FCSTD DOCUMENT  (FreeCAD 0.19R)
Label: Mk8
License: All rights reserved
LicenseURL: http://en.wikipedia.org/wiki/All_rights_reserved
objects: Sketcher::SketchObject×2, PartDesign::Body×1
note: 3 computed .brp shape members not serialized (recipe doc carries the construction recipe); baked Part::Feature solids carry a one-line shape summary decoded from their .brp

FEATURE [Sketcher::SketchObject] Sketch
  FullyConstrained = false
  MapMode = 5
  sketch-geometry (53):
    g0: Circle CenterX=-353.73 CenterY=339.6 CenterZ=0 NormalX=0 NormalY=0 NormalZ=1 AngleXU=0 Radius=339.6
    g1: Circle CenterX=559.315 CenterY=339.6 CenterZ=0 NormalX=0 NormalY=0 NormalZ=1 AngleXU=0 Radius=339.6
    g2: Circle CenterX=0 CenterY=249.6 CenterZ=0 NormalX=0 NormalY=0 NormalZ=1 AngleXU=0 Radius=19
    g3: Circle CenterX=355.046 CenterY=817.792 CenterZ=0 NormalX=0 NormalY=0 NormalZ=1 AngleXU=0 Radius=11.1
    g4: Circle CenterX=0 CenterY=249.6 CenterZ=0 NormalX=0 NormalY=0 NormalZ=1 AngleXU=0 Radius=127
    g5: LineSegment StartX=510.781 StartY=339.6 StartZ=0 EndX=328.385 EndY=791.045 EndZ=0
    g6: LineSegment StartX=559.315 StartY=339.6 StartZ=0 EndX=559.315 EndY=0 EndZ=0
    g7: LineSegment StartX=510.781 StartY=339.6 StartZ=0 EndX=647.988 EndY=0 EndZ=0
    g8: LineSegment StartX=358.792 StartY=808.52 StartZ=0 EndX=324.985 EndY=799.462 EndZ=0
    g9: Circle CenterX=324.985 CenterY=799.462 CenterZ=0 NormalX=0 NormalY=0 NormalZ=1 AngleXU=0 Radius=19
    g10: Circle CenterX=335.796 CenterY=772.703 CenterZ=0 NormalX=0 NormalY=0 NormalZ=1 AngleXU=0 Radius=8
    g11: Circle CenterX=355.65 CenterY=723.562 CenterZ=0 NormalX=0 NormalY=0 NormalZ=1 AngleXU=0 Radius=45
    g12: Circle CenterX=375.13 CenterY=675.348 CenterZ=0 NormalX=0 NormalY=0 NormalZ=1 AngleXU=0 Radius=7
    g13: LineSegment StartX=-353.73 StartY=339.6 StartZ=0 EndX=559.315 EndY=339.6 EndZ=0
    g14: LineSegment StartX=-353.73 StartY=339.6 StartZ=0 EndX=-80.7377 EndY=584.568 EndZ=0
    g15: LineSegment StartX=-13.6879 StartY=474.616 StartZ=0 EndX=345.52 EndY=748.635 EndZ=0
    g16: LineSegment StartX=0 StartY=249.6 StartZ=0 EndX=358.348 EndY=716.885 EndZ=0
    g17: LineSegment StartX=559.315 StartY=0 StartZ=0 EndX=647.988 EndY=0 EndZ=0
    g18: LineSegment StartX=0 StartY=249.6 StartZ=0 EndX=355.046 EndY=817.792 EndZ=0
    g19: LineSegment StartX=-353.73 StartY=339.6 StartZ=0 EndX=0 EndY=249.6 EndZ=0
    g20: LineSegment StartX=355.046 StartY=817.792 StartZ=0 EndX=358.792 EndY=808.52 EndZ=0
    g21: Circle CenterX=332.451 CenterY=780.983 CenterZ=0 NormalX=0 NormalY=0 NormalZ=1 AngleXU=0 Radius=0.930276
    g22: LineSegment StartX=3.73444 StartY=230.971 StartZ=0 EndX=351.145 EndY=683.993 EndZ=0
    g23: LineSegment StartX=3.73444 StartY=230.971 StartZ=0 EndX=351.145 EndY=683.993 EndZ=0
    g24: LineSegment StartX=3.44458 StartY=471.712 StartZ=0 EndX=334.789 EndY=724.476 EndZ=0
    g25: LineSegment StartX=-7.54371 StartY=495.276 StartZ=0 EndX=324.922 EndY=748.896 EndZ=0
    g26: LineSegment StartX=356.409 StartY=772.403 StartZ=0 EndX=321.176 EndY=758.168 EndZ=0
    g27: LineSegment StartX=321.176 StartY=758.168 StartZ=0 EndX=354.891 EndY=674.721 EndZ=0
    g28: LineSegment StartX=354.891 StartY=674.721 StartZ=0 EndX=390.124 EndY=688.956 EndZ=0
    g29: LineSegment StartX=390.124 StartY=688.956 StartZ=0 EndX=356.409 EndY=772.403 EndZ=0
    g30: LineSegment StartX=559.315 StartY=339.6 StartZ=0 EndX=377.752 EndY=668.858 EndZ=0
    g31: LineSegment StartX=63.5524 StartY=308.973 StartZ=0 EndX=-173.714 EndY=817.792 EndZ=0
    g32: LineSegment StartX=329.613 StartY=642.256 StartZ=0 EndX=425.939 EndY=695.372 EndZ=0
    g33: LineSegment StartX=-173.714 StartY=817.792 StartZ=0 EndX=0 EndY=249.6 EndZ=0
    g34: LineSegment StartX=-303.72 StartY=817.792 StartZ=0 EndX=355.046 EndY=817.792 EndZ=0
    g35: LineSegment StartX=53.7404 StartY=296.178 StartZ=0 EndX=-103.376 EndY=633.116 EndZ=0
    g36: LineSegment StartX=-77.3814 StartY=645.043 StartZ=0 EndX=69.984 EndY=329.017 EndZ=0
    g37: LineSegment StartX=481.667 StartY=531.786 StartZ=0 EndX=559.315 EndY=339.6 EndZ=0
    g38: LineSegment StartX=36.0494 StartY=578.413 StartZ=0 EndX=36.0494 EndY=0 EndZ=0
    g39: Circle CenterX=-353.73 CenterY=339.6 CenterZ=0 NormalX=0 NormalY=0 NormalZ=1 AngleXU=0 Radius=327.5
    g40: Circle CenterX=0 CenterY=249.6 CenterZ=0 NormalX=0 NormalY=0 NormalZ=1 AngleXU=0 Radius=21
    g41: LineSegment StartX=-24.7243 StartY=255.437 StartZ=0 EndX=-20.3516 EndY=254.778 EndZ=0
    g42: LineSegment StartX=338.399 StartY=714.37 StartZ=0 EndX=-1.16744 EndY=271.577 EndZ=0
    g43: Circle CenterX=-382.93 CenterY=445.639 CenterZ=0 NormalX=0 NormalY=0 NormalZ=1 AngleXU=0 Radius=8
    g44: LineSegment StartX=-385.819 StartY=453.099 StartZ=0 EndX=325.125 EndY=750.053 EndZ=0
    g45: LineSegment StartX=329.781 StartY=734.661 StartZ=0 EndX=-379.847 EndY=438.257 EndZ=0
    g46: LineSegment StartX=-379.847 StartY=438.257 StartZ=0 EndX=339.437 EndY=716.726 EndZ=0
    g47: LineSegment StartX=-385.819 StartY=453.099 StartZ=0 EndX=330.834 EndY=730.549 EndZ=0
    g48: LineSegment StartX=0 StartY=249.6 StartZ=0 EndX=510.781 EndY=339.6 EndZ=0
    g49: LineSegment StartX=0 StartY=249.6 StartZ=0 EndX=374.387 EndY=681.775 EndZ=0
    g50: LineSegment StartX=510.781 StartY=339.6 StartZ=0 EndX=374.387 EndY=681.775 EndZ=0
    g51: LineSegment StartX=-353.73 StartY=339.6 StartZ=0 EndX=679.043 EndY=281.53 EndZ=0
    g52: LineSegment StartX=527.245 StartY=284.793 StartZ=0 EndX=377.752 EndY=668.858 EndZ=0
  constraints (136):
    c: Radius(g0) = 339.6
    c: Equal(g0,g1)
    c: Radius(g2) = 19
    c: Tangent(g1,g-1)
    c: Tangent(g0,g-1)
    c: Radius(g3) = 11.1
    c: Distance(g2,g3) = 670
    c: Radius(g4) = 127
    c: Coincident(g4,g2)
    c: Distance(g2,g0) = 365
    c: Coincident(g6,g1)
    c: Vertical(g6)
    c: Coincident(g7,g5)
    c: Parallel(g7,g5)
    c: PointOnObject(g8,g5)
    c: Coincident(g9,g8)
    c: Radius(g10) = 8
    c: PointOnObject(g10,g5)
    c: PointOnObject(g11,g5)
    c: Tangent(g11,g10)
    c: Radius(g12) = 7
    c: PointOnObject(g12,g5)
    c: Tangent(g12,g11)
    c: Coincident(g13,g0)
    c: Coincident(g13,g1)
    c: Coincident(g14,g0)
    c: PointOnObject(g15,g5)
    c: Coincident(g16,g2)
    c: PointOnObject(g16,g5)
    c: PointOnObject(g17,g6)
    c: PointOnObject(g17,g7)
    c: Horizontal(g17)
    c: Coincident(g6,g17)
    c: PointOnObject(g6,g-1)
    c: Distance(g2,g13) = 90
    c: Coincident(g18,g2)
    c: Angle(g18) = 1.01229
    c: Distance(g8) = 35
    c: Coincident(g19,g0)
    c: Coincident(g19,g2)
    c: PointOnObject(g2,g-2)
    c: Angle(g5,g8) = 1.44862
    c: Coincident(g20,g8)
    c: Coincident(g18,g20)
    c: Coincident(g3,g18)
    c: Distance(g20) = 10
    c: Parallel(g20,g5)
    c: Radius(g11) = 45
    c: Radius(g9) = 19
    c: PointOnObject(g21,g5)
    c: Tangent(g21,g10)
    c: Tangent(g21,g9)
    c: PointOnObject(g7,g-1)
    c: Parallel(g15,g25)
    c: Parallel(g25,g24)
    c: Parallel(g23,g22)
    c: Parallel(g22,g16)
    c: Distance(g22,g16) = 14.3
    c: Distance(g23,g16) = 14.3
    c: PointOnObject(g22,g2)
    c: PointOnObject(g23,g2)
    c: Distance(g24,g15) = 12.7
    c: Distance(g25,g15) = 12.7
    c: Coincident(g26,g27)
    c: Coincident(g27,g28)
    c: Coincident(g28,g29)
    c: Coincident(g29,g26)
    c: Parallel(g27,g5)
    c: Symmetric(g26,g26,g5)
    c: Symmetric(g28,g27,g5)
    c: Distance(g28,g5) = 19
    c: Tangent(g28,g11)
    c: Tangent(g26,g11)
    c: PointOnObject(g22,g27)
    c: PointOnObject(g25,g27)
    c: Coincident(g30,g1)
    c: PointOnObject(g30,g12)
    c: PointOnObject(g30,g5)
    c: Distance(g30) = 376
    c: Distance(g22,g27) = 10
    c: Distance(g25,g26) = 10
    c: PointOnObject(g5,g13)
    c: Symmetric(g32,g32,g30)
    c: Distance(g32) = 110
    c: Tangent(g32,g12)
    c: PointOnObject(g31,g23)
    c: Coincident(g33,g2)
    c: Angle(g33) = -1.27409
    c: Coincident(g34,g3)
    c: Horizontal(g34)
    c: PointOnObject(g33,g34)
    c: Coincident(g31,g33)
    c: PointOnObject(g35,g23)
    c: Distance(g35,g31) = 14.3
    c: Parallel(g35,g31)
    c: PointOnObject(g23,g27)
    c: Angle(g36) = -1.13446
    c: Parallel(g36,g31)
    c: Distance(g36,g31) = 14.3
    c: Coincident(g37,g1)
    c: Parallel(g5,g37)
    c: Distance(g1,g7) = 45
    c: Angle(g37) = -1.18682
    c: PointOnObject(g24,g27)
    c: PointOnObject(g38,g-1)
    c: Vertical(g38)
    c: Coincident(g39,g0)
    c: Radius(g39) = 327.5
    c: Coincident(g40,g2)
    c: Radius(g40) = 21
    c: PointOnObject(g41,g0)
    c: PointOnObject(g41,g40)
    c: PointOnObject(g41,g19)
    c: PointOnObject(g15,g31)
    c: PointOnObject(g25,g36)
    c: PointOnObject(g24,g36)
    c: Distance(g42,g16) = 14.3
    c: Parallel(g42,g16)
    c: PointOnObject(g14,g35)
    c: Radius(g43) = 8
    c: PointOnObject(g44,g43)
    c: PointOnObject(g45,g43)
    c: Tangent(g45,g43)
    c: Coincident(g46,g45)
    c: Coincident(g47,g44)
    c: Tangent(g47,g43)
    c: Parallel(g46,g47)
    c: Parallel(g45,g44)
    c: Coincident(g48,g2)
    c: Coincident(g48,g5)
    c: Coincident(g49,g2)
    c: Coincident(g50,g5)
    c: Coincident(g50,g49)
    c: Coincident(g51,g0)
    c: Distance(g2,g51) = 70
    c: Coincident(g52,g30)
FEATURE [Sketcher::SketchObject] Sketch001
  FullyConstrained = false
  MapMode = 5
  Support = -> [XY_Plane]
  sketch-geometry (30):
    g0: Circle CenterX=-436674 CenterY=329000 CenterZ=0 NormalX=0 NormalY=0 NormalZ=1 AngleXU=0 Radius=329000
    g1: Circle CenterX=632546 CenterY=329000 CenterZ=0 NormalX=0 NormalY=0 NormalZ=1 AngleXU=0 Radius=329000
    g2: Circle CenterX=0 CenterY=275000 CenterZ=0 NormalX=0 NormalY=0 NormalZ=1 AngleXU=0 Radius=19000
    g3: LineSegment StartX=-436674 StartY=329000 StartZ=0 EndX=0 EndY=275000 EndZ=0
    g4: LineSegment StartX=-134422 StartY=688710 StartZ=0 EndX=0 EndY=275000 EndZ=0
    g5: LineSegment StartX=632546 StartY=329000 StartZ=0 EndX=590535 EndY=312873 EndZ=0
    g6: LineSegment StartX=343612 StartY=956129 StartZ=0 EndX=590535 EndY=312873 EndZ=0
    g7: LineSegment StartX=632546 StartY=329000 StartZ=0 EndX=632546 EndY=0 EndZ=0
    g8: LineSegment StartX=590535 StartY=312873 StartZ=0 EndX=710636 EndY=0 EndZ=0
    g9: LineSegment StartX=632546 StartY=0 StartZ=0 EndX=710636 EndY=0 EndZ=0
    g10: LineSegment StartX=476233 StartY=687378 StartZ=0 EndX=424886 EndY=667668 EndZ=0
    g11: LineSegment StartX=424886 StartY=667668 StartZ=0 EndX=430261 EndY=653664 EndZ=0
    g12: LineSegment StartX=430261 StartY=653664 StartZ=0 EndX=481608 EndY=673374 EndZ=0
    g13: LineSegment StartX=481608 StartY=673374 StartZ=0 EndX=476233 EndY=687378 EndZ=0
    g14: LineSegment StartX=395609 StartY=870901 StartZ=0 EndX=362000 EndY=858000 EndZ=0
    g15: LineSegment StartX=362000 StartY=858000 StartZ=0 EndX=433755 EndY=671072 EndZ=0
    g16: LineSegment StartX=433755 StartY=671072 StartZ=0 EndX=467364 EndY=683974 EndZ=0
    g17: LineSegment StartX=467364 StartY=683974 StartZ=0 EndX=395609 EndY=870901 EndZ=0
    g18: LineSegment StartX=0 StartY=275000 StartZ=0 EndX=420756 EndY=704936 EndZ=0
    g19: LineSegment StartX=381963 StartY=805995 StartZ=0 EndX=-66076.1 EndY=478361 EndZ=0
    g20: LineSegment StartX=-436674 StartY=329000 StartZ=0 EndX=-112971 EndY=622688 EndZ=0
    g21: LineSegment StartX=-193136 StartY=869410 StartZ=0 EndX=-134422 EndY=688710 EndZ=0
    g22: LineSegment StartX=18656.2 StartY=271402 StartZ=0 EndX=427004 EndY=688660 EndZ=0
    g23: LineSegment StartX=414508 StartY=721213 StartZ=0 EndX=-3999.62 EndY=293574 EndZ=0
    g24: LineSegment StartX=9734.18 StartY=291317 StartZ=0 EndX=-111801 EndY=665364 EndZ=0
    g25: LineSegment StartX=-139001 StartY=656526 StartZ=0 EndX=-17466 EndY=282479 EndZ=0
    g26: LineSegment StartX=-57947.1 StartY=499618 StartZ=0 EndX=382859 EndY=824808 EndZ=0
    g27: LineSegment StartX=392082 StartY=796072 StartZ=0 EndX=-48632.1 EndY=470950 EndZ=0
    g28: LineSegment StartX=-144708 StartY=600033 StartZ=0 EndX=-88342.1 EndY=466437 EndZ=0
    g29: LineSegment StartX=-169144 StartY=669579 StartZ=0 EndX=-142386 EndY=604895 EndZ=0
  constraints (75):
    c: Radius(g1) = 329000
    c: Equal(g1,g0)
    c: Tangent(g0,g-1)
    c: Tangent(g1,g-1)
    c: Radius(g2) = 19000
    c: DistanceY(g2) = 275000
    c: Distance(g3) = 440000
    c: Angle(g4) = -1.25664
    c: Distance(g5) = 45000
    c: Angle(g6) = -1.20428
    c: Perpendicular(g6,g5)
    c: PointOnObject(g7,g-1)
    c: Vertical(g7)
    c: PointOnObject(g8,g-1)
    c: Parallel(g8,g6)
    c: Perpendicular(g10,g13)
    c: Coincident(g11,g12)
    c: Parallel(g12,g10)
    c: Coincident(g13,g12)
    c: Symmetric(g10,g10,g6)
    c: Distance(g13) = 15000
    c: Coincident(g10,g13)
    c: Perpendicular(g10,g11)
    c: Coincident(g10,g11)
    c: Distance(g12) = 55000
    c: Coincident(g6,g5)
    c: Coincident(g8,g5)
    c: Coincident(g8,g9)
    c: Coincident(g1,g5)
    c: Coincident(g7,g1)
    c: Coincident(g9,g7)
    c: Distance(g12,g1) = 376000
    c: Coincident(g14,g15)
    c: Coincident(g15,g16)
    c: Coincident(g16,g17)
    c: Coincident(g17,g14)
    c: Symmetric(g14,g14,g6)
    c: Symmetric(g16,g15,g6)
    c: Distance(g16) = 36000
    c: Parallel(g17,g15)
    c: Coincident(g18,g2)
    c: PointOnObject(g18,g15)
    c: PointOnObject(g19,g15)
    c: PointOnObject(g19,g4)
    c: Coincident(g20,g0)
    c: PointOnObject(g20,g4)
    c: DistanceY(g2,g14) = 583000
    c: DistanceX(g4,g14) = 362000
    c: Coincident(g4,g2)
    c: Coincident(g3,g2)
    c: Coincident(g21,g4)
    c: Parallel(g4,g21)
    c: Distance(g21,g2) = 625000
    c: Coincident(g3,g0)
    c: PointOnObject(g2,g-2)
    c: Distance(g21) = 190000
    c: PointOnObject(g22,g2)
    c: PointOnObject(g22,g15)
    c: PointOnObject(g23,g15)
    c: Distance(g22,g23) = 31700
    c: Symmetric(g22,g23,g18)
    c: Parallel(g22,g18)
    c: Parallel(g23,g18)
    c: Distance(g24,g25) = 28600
    c: Symmetric(g24,g25,g4)
    c: Distance(g24,g25) = 28600
    c: Symmetric(g24,g25,g4)
    c: PointOnObject(g26,g24)
    c: PointOnObject(g27,g24)
    c: Distance(g27,g26) = 28600
    c: Distance(g27,g26) = 28600
    c: PointOnObject(g16,g10)
    c: Distance(g28) = 145000
    c: Distance(g29) = 70000
    c: PointOnObject(g24,g2)
FEATURE [PartDesign::Body] Body
  Group = -> [Sketch001]
  Origin = -> Origin
